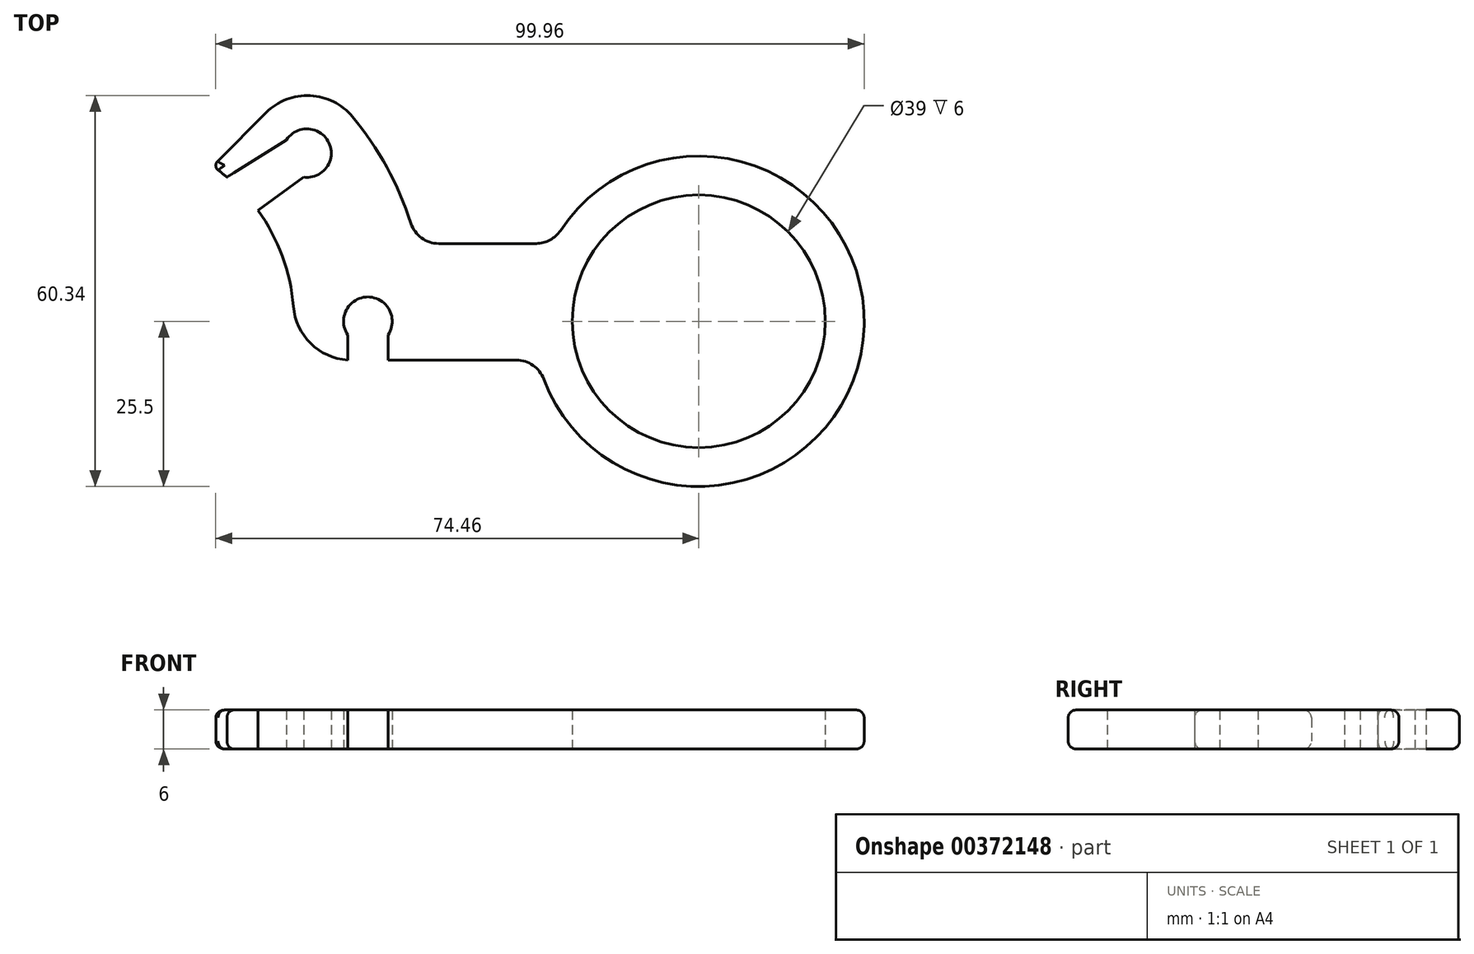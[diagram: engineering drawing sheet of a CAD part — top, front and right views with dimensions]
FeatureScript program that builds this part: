
annotation { "Feature Type Name" : "Feature", "Feature Type Description" : "" }
export const myFeature = defineFeature(function(context is Context, id is Id, definition is map)
    precondition{}
    {
        {
            var Q0;
            Q0=qCreatedBy(makeId("Top.planeOp"),FACE);
            var sketch = newSketch(context, id + "F0", { "sketchPlane" : qUnion([Q0])});
            skCircle(sketch, "E0", {"center": v(0, 0) * mm, "radius": 13.5 * mm, "construction": true});
            skCircle(sketch, "E1", {"center": v(13.5, 0) * mm, "radius": 9.2 * mm, "construction": true});
            skLineSegment(sketch, "E2", {"start": v(10.37, 8.65) * mm, "end": v(-2.46, 0) * mm, "construction": true});
            skArc(sketch, "E3", {"start": v(9.67, 0.76) * mm, "mid": v(9.1, 3.36) * mm, "end": v(7.85, 5.7) * mm});
            skArc(sketch, "E4", {"start": v(15.71, 5.04) * mm, "mid": v(14.47, 7.93) * mm, "end": v(12.7, 10.53) * mm});
            skCircle(sketch, "E5", {"center": v(30.5, 0) * mm, "radius": 6.5 * mm});
            skArc(sketch, "E6", {"start": v(22.54, -2.98) * mm, "mid": v(38.95, -0.95) * mm, "end": v(23.4, 4.68) * mm});
            skLineSegment(sketch, "E7", {"start": v(12.47, -2) * mm, "end": v(12.66, -2) * mm});
            skLineSegment(sketch, "E8", {"start": v(5.77, 8.23) * mm, "end": v(8.28, 10.73) * mm});
            skArc(sketch, "E9", {"start": v(10.2, 7.41) * mm, "mid": v(11.5, 9.17) * mm, "end": v(9.32, 9.33) * mm});
            skArc(sketch, "E10", {"start": v(14.53, -0.7) * mm, "mid": v(13.5, 1.25) * mm, "end": v(12.47, -0.7) * mm});
            skLineSegment(sketch, "E11", {"start": v(12.47, -0.7) * mm, "end": v(12.47, -2) * mm});
            skLineSegment(sketch, "E12", {"start": v(14.53, -0.7) * mm, "end": v(14.53, -2) * mm});
            skLineSegment(sketch, "E13.trimOffspring", {"start": v(14.53, -2) * mm, "end": v(21.13, -2) * mm});
            skLineSegment(sketch, "E14", {"start": v(17.14, 4) * mm, "end": v(22.15, 4) * mm});
            skLineSegment(sketch, "E15", {"start": v(0, 0) * mm, "end": v(10.2, 7.41) * mm});
            skLineSegment(sketch, "E16", {"start": v(9.32, 9.33) * mm, "end": v(6.35, 7.33) * mm, "construction": true});
            skLineSegment(sketch, "E17", {"start": v(9.32, 9.33) * mm, "end": v(6.25, 7.42) * mm});
            skArc(sketch, "E18.trimOffspring", {"start": v(6.25, 7.42) * mm, "mid": v(6.03, 7.6) * mm, "end": v(5.8, 7.77) * mm});
            skPoint(sketch, "E19.visualSharp", {"position": v(10.37, 12.83) * mm});
            skArc(sketch, "E19.filletArc", {"start": v(12.7, 10.53) * mm, "mid": v(10.54, 11.6) * mm, "end": v(8.28, 10.73) * mm});
            skPoint(sketch, "E20.visualSharp", {"position": v(9.5, -2) * mm});
            skArc(sketch, "E20.filletArc", {"start": v(9.67, 0.76) * mm, "mid": v(10.62, -1.2) * mm, "end": v(12.66, -2) * mm});
            skPoint(sketch, "E21.visualSharp", {"position": v(23, 4) * mm});
            skArc(sketch, "E21.filletArc", {"start": v(22.15, 4) * mm, "mid": v(22.86, 4.18) * mm, "end": v(23.4, 4.67) * mm});
            skPoint(sketch, "E22.visualSharp", {"position": v(22.24, -2) * mm});
            skArc(sketch, "E22.filletArc", {"start": v(22.54, -2.97) * mm, "mid": v(21.99, -2.27) * mm, "end": v(21.13, -2) * mm});
            skPoint(sketch, "E23.visualSharp", {"position": v(16, 4) * mm});
            skArc(sketch, "E23.filletArc", {"start": v(15.71, 5.04) * mm, "mid": v(16.26, 4.29) * mm, "end": v(17.14, 4) * mm});
            skPoint(sketch, "E24.visualSharp", {"position": v(5.52, 7.98) * mm});
            skArc(sketch, "E24.filletArc", {"start": v(5.77, 8.23) * mm, "mid": v(5.68, 8) * mm, "end": v(5.8, 7.77) * mm});
            skLineSegment(sketch, "E25", {"start": v(13.5, 0) * mm, "end": v(13.5, -2) * mm, "construction": true});
            skSolve(sketch);
        }
        {
            var Q0;
            {var subQ3=sQuery(id+"F0.wireOp",EDGE,"E7");var subQ6=sQuery(id+"F0.wireOp",EDGE,"E3");Q0=qUnion([makeQuery(id+"F0.imprint","IMPRINT",FACE,{"disambiguationData":[TD([[makeQuery(id+"F0.imprint","IMPRINT",EDGE,{"derivedFrom":subQ3}),1.0]])]}),makeQuery(id+"F0.imprint","IMPRINT",FACE,{"disambiguationData":[TD([[makeQuery(id+"F0.imprint","IMPRINT",EDGE,{"derivedFrom":subQ6}),-1.0]])]})]);}
            extrude(context, id + "F1", {"entities" : qUnion([Q0]), "depth" : 2 * mm});
        }
        {
            var Q0;
            Q0=makeQuery(id+"F1.opExtrude","CAP_EDGE",EDGE,{"disambiguationData":[OSD([sQuery(id+"F0.wireOp",EDGE,"E13.trimOffspring")])],"isStart":false});
            var Q1;
            Q1=makeQuery(id+"F1.opExtrude","CAP_EDGE",EDGE,{"disambiguationData":[OSD([sQuery(id+"F0.wireOp",EDGE,"E13.trimOffspring")])],"isStart":true});
            fillet(context, id + "F2", {"entities" : qUnion([Q0, Q1]), "radius" : 0.4 * mm, "tangentPropagation" : true, "allowEdgeOverflow" : false});
        }
        {
            var Q0;
            Q0=makeQuery(id+"F1.opExtrude","SWEPT_BODY",BODY,{"disambiguationData":[OSD([sQuery(id+"F0.wireOp",EDGE,"E7"),sQuery(id+"F0.wireOp",EDGE,"E11"),sQuery(id+"F0.wireOp",EDGE,"E20.filletArc")])]});
            deleteBodies(context, id + "F3", {"entities" : qUnion([Q0])});
        }
        {
            var Q0;
            Q0=makeQuery(id+"F1.opExtrude","SWEPT_BODY",BODY,{"disambiguationData":[OSD([sQuery(id+"F0.wireOp",EDGE,"E3"),sQuery(id+"F0.wireOp",EDGE,"E4"),sQuery(id+"F0.wireOp",EDGE,"E5"),sQuery(id+"F0.wireOp",EDGE,"E6"),sQuery(id+"F0.wireOp",EDGE,"E8"),sQuery(id+"F0.wireOp",EDGE,"E9"),sQuery(id+"F0.wireOp",EDGE,"E10"),sQuery(id+"F0.wireOp",EDGE,"E11"),sQuery(id+"F0.wireOp",EDGE,"E12"),sQuery(id+"F0.wireOp",EDGE,"E13.trimOffspring"),sQuery(id+"F0.wireOp",EDGE,"E14"),sQuery(id+"F0.wireOp",EDGE,"E15"),sQuery(id+"F0.wireOp",EDGE,"E17"),sQuery(id+"F0.wireOp",EDGE,"E18.trimOffspring"),sQuery(id+"F0.wireOp",EDGE,"E19.filletArc"),sQuery(id+"F0.wireOp",EDGE,"E20.filletArc"),sQuery(id+"F0.wireOp",EDGE,"E21.filletArc"),sQuery(id+"F0.wireOp",EDGE,"E22.filletArc"),sQuery(id+"F0.wireOp",EDGE,"E23.filletArc"),sQuery(id+"F0.wireOp",EDGE,"E24.filletArc")])]});
            var Q1;
            Q1=qCreatedBy(makeId("Origin.pointOp"),VERTEX);
            transform(context, id + "F4", {"entities" : qUnion([Q0]), "transformType" : TransformType.SCALE_UNIFORMLY, "scale" : 3, "makeCopy" : false, "scalePoint" : qUnion([Q1])});
        }
    });
